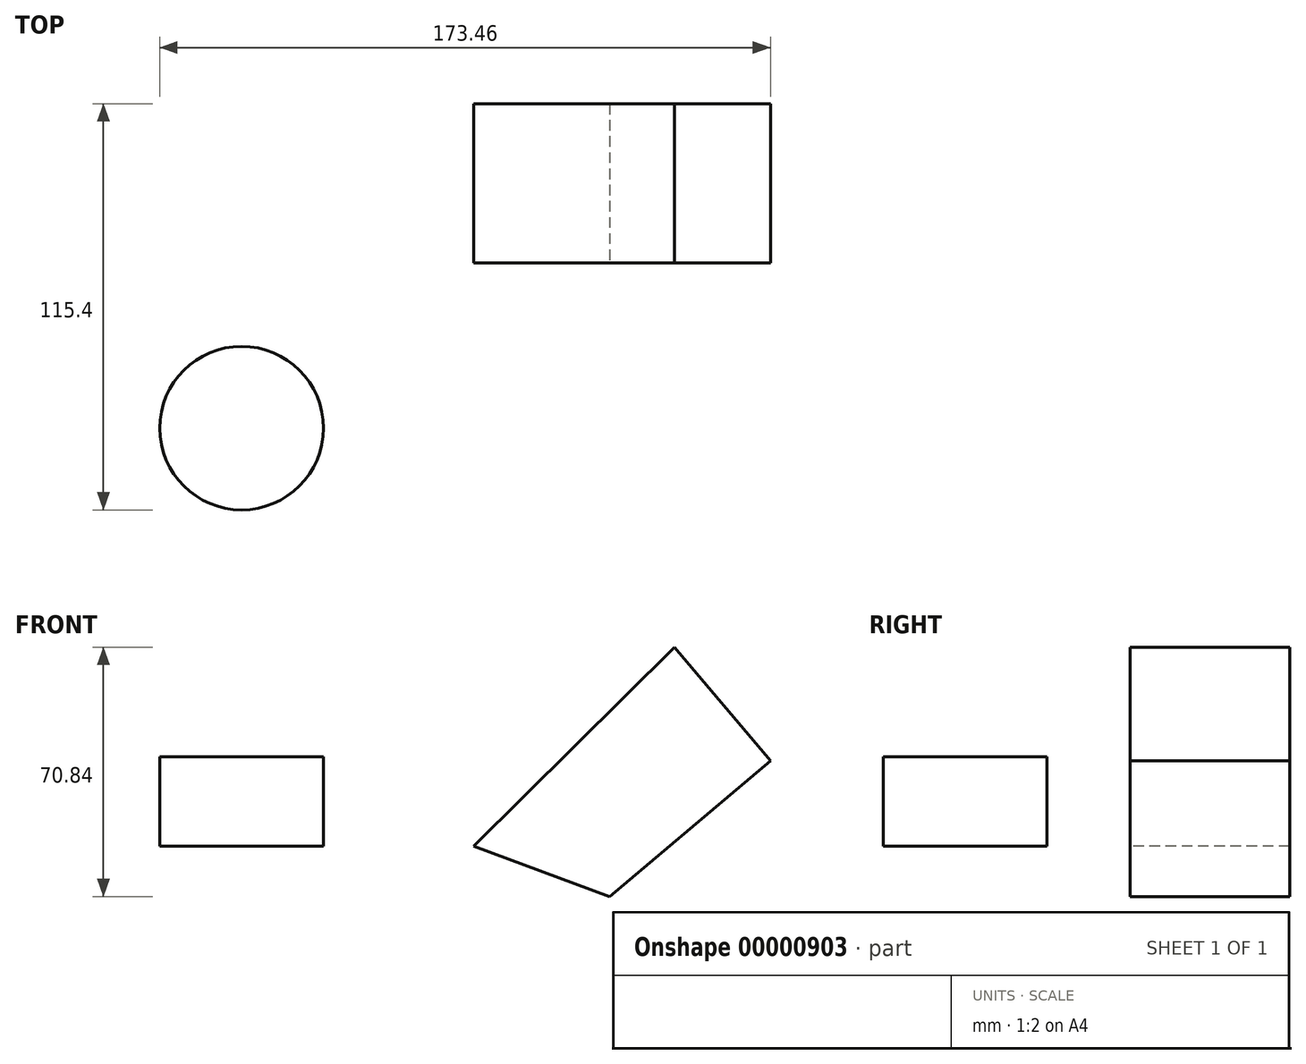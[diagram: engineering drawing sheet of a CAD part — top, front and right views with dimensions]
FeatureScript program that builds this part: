
annotation { "Feature Type Name" : "Feature", "Feature Type Description" : "" }
export const myFeature = defineFeature(function(context is Context, id is Id, definition is map)
    precondition{}
    {
        {
            var Q0;
            Q0=qCreatedBy(makeId("Front.planeOp"),FACE);
            var sketch = newSketch(context, id + "F0", { "sketchPlane" : qUnion([Q0])});
            skLineSegment(sketch, "E0", {"start": v(0, 0) * mm, "end": v(57.03, 56.5) * mm});
            skLineSegment(sketch, "E1", {"start": v(57.03, 56.5) * mm, "end": v(84.3, 24.17) * mm});
            skLineSegment(sketch, "E2", {"start": v(84.3, 24.17) * mm, "end": v(38.65, -14.33) * mm});
            skLineSegment(sketch, "E3", {"start": v(38.65, -14.33) * mm, "end": v(0, 0) * mm});
            skSolve(sketch);
        }
        {
            var Q0;
            Q0=makeQuery(id+"F0.imprint","IMPRINT",FACE,{"disambiguationData":[TD([[makeQuery(id+"F0.imprint","IMPRINT",EDGE,{"derivedFrom":sQuery(id+"F0.wireOp",EDGE,"E0")}),-1.0]])]});
            extrude(context, id + "F1", {"entities" : qUnion([Q0]), "oppositeDirection" : true, "depth" : 45.22 * mm});
        }
        {
            var Q0;
            Q0=qCreatedBy(makeId("Top.planeOp"),FACE);
            var sketch = newSketch(context, id + "F2", { "sketchPlane" : qUnion([Q0])});
            skCircle(sketch, "E4", {"center": v(-65.91, -46.93) * mm, "radius": 23.24 * mm});
            skSolve(sketch);
        }
        {
            var Q0;
            Q0=makeQuery(id+"F2.imprint","IMPRINT",FACE,{"disambiguationData":[TD([[makeQuery(id+"F2.imprint","IMPRINT",EDGE,{"derivedFrom":sQuery(id+"F2.wireOp",EDGE,"E4")}),1.0]])]});
            extrude(context, id + "F3", {"entities" : qUnion([Q0]), "depth" : 25.4 * mm});
        }
    });
